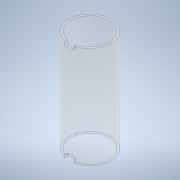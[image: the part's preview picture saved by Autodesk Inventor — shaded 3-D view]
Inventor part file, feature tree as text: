
AUTODESK INVENTOR PART (.ipt)
format: ipt  version: 2022 (Build 260153000, 153)  size: 141,312 bytes
history: native  units: in
note: dims shown in document units (in); Inventor stores cm internally (conversion verified against a paired STEP export)
features: sketch x2, extrude x1, revolve x1, fillet x1
ambient origin geometry x8: Origin, YZ Plane, XZ Plane, XY Plane, X Axis, Y Axis, Z Axis, Center Point
bodies: Body1 (feature_tree)
feature tree (5):
  extrude  "Extrusion3"  Depth=2.0315in
  revolve  "Revolution2"  [1 undecoded]
  fillet  "Fillet3"  Radius=0.1575in
  sketch  "Sketch5"  dims[d26=2.2677in d27=2.0315in]
  sketch  "Sketch6"  dims[d28=5.4488in d29=0.0in d31=0.2205in d32=0.1575in d33=0.2205in d34=0.1575in d35=0.086in d36=0.086in d37=0.0787in]
note: 1 required parameter value undecoded (feature->parameter linkage not recoverable at this tier; creation-order binding heuristic only, values carry confidence <= 0.55)
